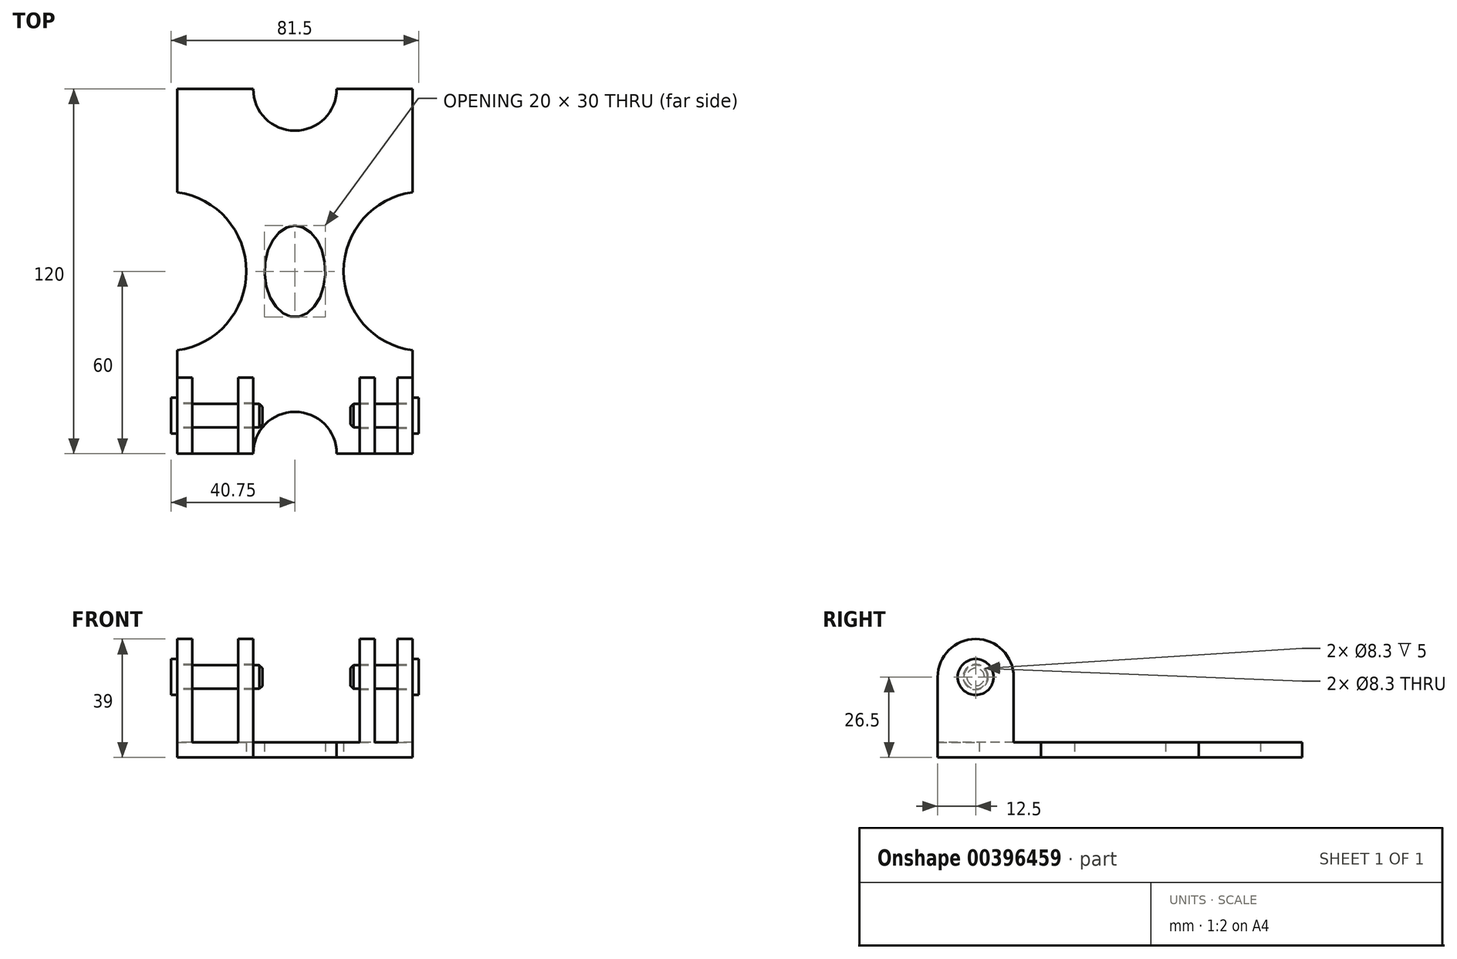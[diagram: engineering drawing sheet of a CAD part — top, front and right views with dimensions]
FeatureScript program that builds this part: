
annotation { "Feature Type Name" : "Feature", "Feature Type Description" : "" }
export const myFeature = defineFeature(function(context is Context, id is Id, definition is map)
    precondition{}
    {
        {
            assignVariable(context, id + "F0", {"name" : "bearing_plate_spacing", "anyValue" : 7.5});
        }
        {
            assignVariable(context, id + "F1", {"name" : "bearing_plate_thickness", "anyValue" : 5});
        }
        {
            var Q0;
            Q0=qCreatedBy(makeId("Top.planeOp"),FACE);
            var sketch = newSketch(context, id + "F2", { "sketchPlane" : qUnion([Q0])});
            skEllipse(sketch, "E0", {"center": v(0, 0) * mm, "majorRadius": 15 * mm, "minorRadius": 10 * mm, "majorAxis": v(0, 1)});
            skArc(sketch, "E1", {"start": v(16, 0) * mm, "mid": v(22.5, -17.27) * mm, "end": v(38.75, -26) * mm});
            skLineSegment(sketch, "E2", {"start": v(38.75, -26) * mm, "end": v(38.75, -60) * mm});
            skLineSegment(sketch, "E3", {"start": v(38.75, -60) * mm, "end": v(13.75, -60) * mm});
            skArc(sketch, "E4", {"start": v(13.75, -60) * mm, "mid": v(9.72, -50.28) * mm, "end": v(0, -46.25) * mm});
            skLineSegment(sketch, "E5", {"start": v(0, 28.48) * mm, "end": v(0, -32) * mm, "construction": true});
            skLineSegment(sketch, "E6", {"start": v(-23.98, 0) * mm, "end": v(29.2, 0) * mm, "construction": true});
            skArc(sketch, "E7.MirrorCS", {"start": v(-16, 0) * mm, "mid": v(-22.5, -17.27) * mm, "end": v(-38.75, -26) * mm});
            skLineSegment(sketch, "E8.MirrorCS", {"start": v(-38.75, -60) * mm, "end": v(-13.75, -60) * mm});
            skLineSegment(sketch, "E9.MirrorCS", {"start": v(-38.75, -26) * mm, "end": v(-38.75, -60) * mm});
            skArc(sketch, "E10.MirrorCS", {"start": v(-13.75, -60) * mm, "mid": v(-9.72, -50.28) * mm, "end": v(0, -46.25) * mm});
            skArc(sketch, "E11.MirrorCS", {"start": v(16, 0) * mm, "mid": v(22.5, 17.27) * mm, "end": v(38.75, 26) * mm});
            skLineSegment(sketch, "E12.MirrorCS", {"start": v(38.75, 26) * mm, "end": v(38.75, 60) * mm});
            skLineSegment(sketch, "E13.MirrorCS", {"start": v(38.75, 60) * mm, "end": v(13.75, 60) * mm});
            skArc(sketch, "E14.MirrorCS", {"start": v(13.75, 60) * mm, "mid": v(9.72, 50.28) * mm, "end": v(0, 46.25) * mm});
            skArc(sketch, "E15.MirrorCS", {"start": v(-13.75, 60) * mm, "mid": v(-9.72, 50.28) * mm, "end": v(0, 46.25) * mm});
            skLineSegment(sketch, "E16.MirrorCS", {"start": v(-38.75, 60) * mm, "end": v(-13.75, 60) * mm});
            skLineSegment(sketch, "E17.MirrorCS", {"start": v(-38.75, 26) * mm, "end": v(-38.75, 60) * mm});
            skArc(sketch, "E18.MirrorCS", {"start": v(-16, 0) * mm, "mid": v(-22.5, 17.27) * mm, "end": v(-38.75, 26) * mm});
            skLineSegment(sketch, "E19", {"start": v(10, 0) * mm, "end": v(10, 8.76) * mm, "construction": true});
            skLineSegment(sketch, "E20", {"start": v(16, 0) * mm, "end": v(16, 7.85) * mm, "construction": true});
            skSolve(sketch);
        }
        {
            var Q0;
            Q0 = qSketchRegion(id + "F2", true);
            extrude(context, id + "F3", {"entities" : qUnion([Q0]), "depth" : 5 * mm});
        }
        {
            var Q0;
            Q0=qCreatedBy(makeId("Right.planeOp"),FACE);
            var sketch = newSketch(context, id + "F4", { "sketchPlane" : qUnion([Q0])});
            skLineSegment(sketch, "E21.0", {"start": v(-26, 5) * mm, "end": v(-60, 5) * mm, "construction": true});
            skLineSegment(sketch, "E22", {"start": v(-60, 5) * mm, "end": v(-60, 26.5) * mm});
            skLineSegment(sketch, "E23", {"start": v(-35, 5) * mm, "end": v(-35, 26.5) * mm});
            skLineSegment(sketch, "E24", {"start": v(-60, 5) * mm, "end": v(-35, 5) * mm});
            skArc(sketch, "E25", {"start": v(-35, 26.5) * mm, "mid": v(-47.5, 39) * mm, "end": v(-60, 26.5) * mm});
            skCircle(sketch, "E26", {"center": v(-47.5, 26.5) * mm, "radius": 4.15 * mm});
            skSolve(sketch);
        }
        {
            var Q0;
            Q0=makeQuery(id+"F3.opExtrude","SWEPT_FACE",FACE,{"disambiguationData":[OSD([sQuery(id+"F2.wireOp",EDGE,"E2")])]});
            cPlane(context, id + "F5", {"entities" : qUnion([Q0]), "cplaneType" : CPlaneType.OFFSET, "offset" : 0 * mm, "width" : 150 * mm, "height" : 150 * mm});
        }
        {
            var Q0;
            Q0=qCreatedBy(id+"F5.planeOp",FACE);
            var sketch = newSketch(context, id + "F6", { "sketchPlane" : qUnion([Q0])});
            skLineSegment(sketch, "E27.0", {"start": v(-26, 5) * mm, "end": v(-60, 5) * mm});
            skLineSegment(sketch, "E27.1", {"start": v(-60, 5) * mm, "end": v(-60, 26.5) * mm});
            skLineSegment(sketch, "E27.2", {"start": v(-35, 5) * mm, "end": v(-35, 26.5) * mm});
            skLineSegment(sketch, "E27.3", {"start": v(-60, 5) * mm, "end": v(-35, 5) * mm});
            skArc(sketch, "E27.4", {"start": v(-35, 26.5) * mm, "mid": v(-47.5, 39) * mm, "end": v(-60, 26.5) * mm});
            skCircle(sketch, "E28.0", {"center": v(-47.5, 26.5) * mm, "radius": 4.15 * mm});
            skSolve(sketch);
        }
        {
            var Q0;
            Q0 = qSketchRegion(id + "F6", true);
            extrude(context, id + "F7", {"entities" : qUnion([Q0]), "operationType" : NewBodyOperationType.ADD, "oppositeDirection" : true, "depth" : (getVariable(context, 'bearing_plate_thickness')) * mm});
        }
        {
            var Q0;
            Q0=makeQuery(id+"F3.opExtrude","SWEPT_FACE",FACE,{"disambiguationData":[OSD([sQuery(id+"F2.wireOp",EDGE,"E2")])]});
            cPlane(context, id + "F8", {"entities" : qUnion([Q0]), "cplaneType" : CPlaneType.OFFSET, "offset" : (getVariable(context, 'bearing_plate_thickness') + getVariable(context, 'bearing_plate_spacing')) * mm, "oppositeDirection" : true, "width" : 150 * mm, "height" : 150 * mm});
        }
        {
            var Q0;
            Q0=qCreatedBy(id+"F8.planeOp",FACE);
            var sketch = newSketch(context, id + "F9", { "sketchPlane" : qUnion([Q0])});
            skLineSegment(sketch, "E29.0", {"start": v(-26, 5) * mm, "end": v(-60, 5) * mm});
            skLineSegment(sketch, "E29.1", {"start": v(-60, 5) * mm, "end": v(-60, 26.5) * mm});
            skLineSegment(sketch, "E29.2", {"start": v(-35, 5) * mm, "end": v(-35, 26.5) * mm});
            skLineSegment(sketch, "E29.3", {"start": v(-60, 5) * mm, "end": v(-35, 5) * mm});
            skArc(sketch, "E29.4", {"start": v(-35, 26.5) * mm, "mid": v(-47.5, 39) * mm, "end": v(-60, 26.5) * mm});
            skCircle(sketch, "E30.0", {"center": v(-47.5, 26.5) * mm, "radius": 4.15 * mm});
            skSolve(sketch);
        }
        {
            var Q0;
            Q0 = qSketchRegion(id + "F9", true);
            extrude(context, id + "F10", {"entities" : qUnion([Q0]), "operationType" : NewBodyOperationType.ADD, "oppositeDirection" : true, "depth" : (getVariable(context, 'bearing_plate_thickness')) * mm});
        }
        {
            var Q0;
            Q0=makeQuery(id+"F3.opExtrude","SWEPT_FACE",FACE,{"disambiguationData":[OSD([sQuery(id+"F2.wireOp",EDGE,"E9.MirrorCS")])]});
            cPlane(context, id + "F11", {"entities" : qUnion([Q0]), "cplaneType" : CPlaneType.OFFSET, "offset" : 0 * mm, "width" : 150 * mm, "height" : 150 * mm});
        }
        {
            var Q0;
            Q0=makeQuery(id+"F3.opExtrude","SWEPT_FACE",FACE,{"disambiguationData":[OSD([sQuery(id+"F2.wireOp",EDGE,"E9.MirrorCS")])]});
            cPlane(context, id + "F12", {"entities" : qUnion([Q0]), "cplaneType" : CPlaneType.OFFSET, "offset" : (getVariable(context, 'bearing_plate_thickness') + 2 * getVariable(context, 'bearing_plate_spacing')) * mm, "oppositeDirection" : true, "width" : 150 * mm, "height" : 150 * mm});
        }
        {
            var Q0;
            Q0=qCreatedBy(id+"F11.planeOp",FACE);
            var sketch = newSketch(context, id + "F13", { "sketchPlane" : qUnion([Q0])});
            skLineSegment(sketch, "E31.0", {"start": v(26, 5) * mm, "end": v(60, 5) * mm});
            skLineSegment(sketch, "E31.1", {"start": v(60, 5) * mm, "end": v(60, 26.5) * mm});
            skLineSegment(sketch, "E31.2", {"start": v(35, 5) * mm, "end": v(35, 26.5) * mm});
            skLineSegment(sketch, "E31.3", {"start": v(60, 5) * mm, "end": v(35, 5) * mm});
            skArc(sketch, "E31.4", {"start": v(35, 26.5) * mm, "mid": v(47.5, 39) * mm, "end": v(60, 26.5) * mm});
            skCircle(sketch, "E32.0", {"center": v(47.5, 26.5) * mm, "radius": 4.15 * mm});
            skSolve(sketch);
        }
        {
            var Q0;
            Q0 = qSketchRegion(id + "F13", true);
            extrude(context, id + "F14", {"entities" : qUnion([Q0]), "operationType" : NewBodyOperationType.ADD, "oppositeDirection" : true, "depth" : (getVariable(context, 'bearing_plate_thickness')) * mm});
        }
        {
            var Q0;
            Q0=qCreatedBy(id+"F12.planeOp",FACE);
            var sketch = newSketch(context, id + "F15", { "sketchPlane" : qUnion([Q0])});
            skLineSegment(sketch, "E33.0", {"start": v(26, 5) * mm, "end": v(60, 5) * mm});
            skLineSegment(sketch, "E33.1", {"start": v(60, 5) * mm, "end": v(60, 26.5) * mm});
            skLineSegment(sketch, "E33.2", {"start": v(35, 5) * mm, "end": v(35, 26.5) * mm});
            skLineSegment(sketch, "E33.3", {"start": v(60, 5) * mm, "end": v(35, 5) * mm});
            skArc(sketch, "E33.4", {"start": v(35, 26.5) * mm, "mid": v(47.5, 39) * mm, "end": v(60, 26.5) * mm});
            skCircle(sketch, "E34.0", {"center": v(47.5, 26.5) * mm, "radius": 4.15 * mm});
            skSolve(sketch);
        }
        {
            var Q0;
            Q0 = qSketchRegion(id + "F15", true);
            extrude(context, id + "F16", {"entities" : qUnion([Q0]), "operationType" : NewBodyOperationType.ADD, "oppositeDirection" : true, "depth" : (getVariable(context, 'bearing_plate_thickness')) * mm});
        }
        {
            var Q0;
            Q0=makeQuery(id+"F7.boolean.opBoolean","MERGE",FACE,{"derivedFrom":[makeQuery(id+"F3.opExtrude","SWEPT_FACE",FACE,{"disambiguationData":[OSD([sQuery(id+"F2.wireOp",EDGE,"E2")])]}),makeQuery(id+"F7.opExtrude","CAP_FACE",FACE,{"disambiguationData":[OSD([sQuery(id+"F6.wireOp",EDGE,"E27.1"),sQuery(id+"F6.wireOp",EDGE,"E27.2"),sQuery(id+"F6.wireOp",EDGE,"E27.3"),sQuery(id+"F6.wireOp",EDGE,"E27.4"),sQuery(id+"F6.wireOp",EDGE,"E28.0")])],"isStart":true})]});
            var sketch = newSketch(context, id + "F17", { "sketchPlane" : qUnion([Q0])});
            skCircle(sketch, "E35.0", {"center": v(-47.5, 26.5) * mm, "radius": 4.15 * mm, "construction": true});
            skCircle(sketch, "E36", {"center": v(-47.5, 26.5) * mm, "radius": 3.9 * mm});
            skSolve(sketch);
        }
        {
            var Q0;
            Q0 = qSketchRegion(id + "F17", true);
            var Q1;
            Q1=makeQuery(id+"F10.opExtrude","CAP_FACE",FACE,{"disambiguationData":[OSD([sQuery(id+"F9.wireOp",EDGE,"E29.1"),sQuery(id+"F9.wireOp",EDGE,"E29.2"),sQuery(id+"F9.wireOp",EDGE,"E29.3"),sQuery(id+"F9.wireOp",EDGE,"E29.4"),sQuery(id+"F9.wireOp",EDGE,"E30.0")])],"isStart":false});
            extrude(context, id + "F18", {"entities" : qUnion([Q0]), "endBound" : BoundingType.UP_TO_SURFACE, "oppositeDirection" : true, "depth" : 25 * mm, "endBoundEntityFace" : qUnion([Q1]), "hasOffset" : true, "offsetDistance" : 3 * mm, "offsetOppositeDirection" : true});
        }
        {
            var Q0;
            Q0=makeQuery(id+"F18.opExtrude","CAP_FACE",FACE,{"disambiguationData":[OSD([sQuery(id+"F17.wireOp",EDGE,"E36")])],"isStart":true});
            var sketch = newSketch(context, id + "F19", { "sketchPlane" : qUnion([Q0])});
            skCircle(sketch, "E37.0", {"center": v(-47.5, 26.5) * mm, "radius": 3.9 * mm, "construction": true});
            skCircle(sketch, "E38", {"center": v(-47.5, 26.5) * mm, "radius": 5.9 * mm});
            skSolve(sketch);
        }
        {
            var Q0;
            Q0 = qSketchRegion(id + "F19", true);
            extrude(context, id + "F20", {"entities" : qUnion([Q0]), "operationType" : NewBodyOperationType.ADD, "depth" : 2 * mm, "offsetDistance" : 25 * mm});
        }
        {
            var Q0;
            Q0=makeQuery(id+"F14.boolean.opBoolean","MERGE",FACE,{"derivedFrom":[makeQuery(id+"F3.opExtrude","SWEPT_FACE",FACE,{"disambiguationData":[OSD([sQuery(id+"F2.wireOp",EDGE,"E9.MirrorCS")])]}),makeQuery(id+"F14.opExtrude","CAP_FACE",FACE,{"disambiguationData":[OSD([sQuery(id+"F13.wireOp",EDGE,"E31.1"),sQuery(id+"F13.wireOp",EDGE,"E31.2"),sQuery(id+"F13.wireOp",EDGE,"E31.3"),sQuery(id+"F13.wireOp",EDGE,"E31.4"),sQuery(id+"F13.wireOp",EDGE,"E32.0")])],"isStart":true})]});
            var sketch = newSketch(context, id + "F21", { "sketchPlane" : qUnion([Q0])});
            skCircle(sketch, "E39", {"center": v(47.5, 26.5) * mm, "radius": 3.9 * mm});
            skCircle(sketch, "E40.0", {"center": v(47.5, 26.5) * mm, "radius": 4.15 * mm, "construction": true});
            skSolve(sketch);
        }
        {
            var Q0;
            Q0 = qSketchRegion(id + "F21", true);
            var Q1;
            Q1=makeQuery(id+"F16.opExtrude","CAP_FACE",FACE,{"disambiguationData":[OSD([sQuery(id+"F15.wireOp",EDGE,"E33.1"),sQuery(id+"F15.wireOp",EDGE,"E33.2"),sQuery(id+"F15.wireOp",EDGE,"E33.3"),sQuery(id+"F15.wireOp",EDGE,"E33.4"),sQuery(id+"F15.wireOp",EDGE,"E34.0")])],"isStart":false});
            extrude(context, id + "F22", {"entities" : qUnion([Q0]), "endBound" : BoundingType.UP_TO_SURFACE, "oppositeDirection" : true, "depth" : 25 * mm, "endBoundEntityFace" : qUnion([Q1]), "hasOffset" : true, "offsetDistance" : 3 * mm, "offsetOppositeDirection" : true});
        }
        {
            var Q0;
            Q0=makeQuery(id+"F22.opExtrude","CAP_FACE",FACE,{"disambiguationData":[OSD([sQuery(id+"F21.wireOp",EDGE,"E39")])],"isStart":true});
            var sketch = newSketch(context, id + "F23", { "sketchPlane" : qUnion([Q0])});
            skCircle(sketch, "E41.0", {"center": v(47.5, 26.5) * mm, "radius": 3.9 * mm, "construction": true});
            skCircle(sketch, "E42", {"center": v(47.5, 26.5) * mm, "radius": 5.9 * mm});
            skSolve(sketch);
        }
        {
            var Q0;
            Q0 = qSketchRegion(id + "F23", true);
            extrude(context, id + "F24", {"entities" : qUnion([Q0]), "operationType" : NewBodyOperationType.ADD, "depth" : 2 * mm, "offsetDistance" : 25 * mm});
        }
        {
            var Q0;
            Q0=makeQuery(id+"F18.opExtrude","CAP_EDGE",EDGE,{"disambiguationData":[OSD([sQuery(id+"F17.wireOp",EDGE,"E36")])],"isStart":false});
            var Q1;
            Q1=makeQuery(id+"F18.opExtrude","CAP_EDGE",EDGE,{"disambiguationData":[OSD([sQuery(id+"F17.wireOp",EDGE,"E36")])],"isStart":true});
            var Q2;
            Q2=makeQuery(id+"F22.opExtrude","CAP_EDGE",EDGE,{"disambiguationData":[OSD([sQuery(id+"F21.wireOp",EDGE,"E39")])],"isStart":true});
            var Q3;
            Q3=makeQuery(id+"F22.opExtrude","CAP_EDGE",EDGE,{"disambiguationData":[OSD([sQuery(id+"F21.wireOp",EDGE,"E39")])],"isStart":false});
            chamfer(context, id + "F25", {"entities" : qUnion([Q0, Q1, Q2, Q3]), "width" : 1 * mm, "tangentPropagation" : true});
        }
    });
